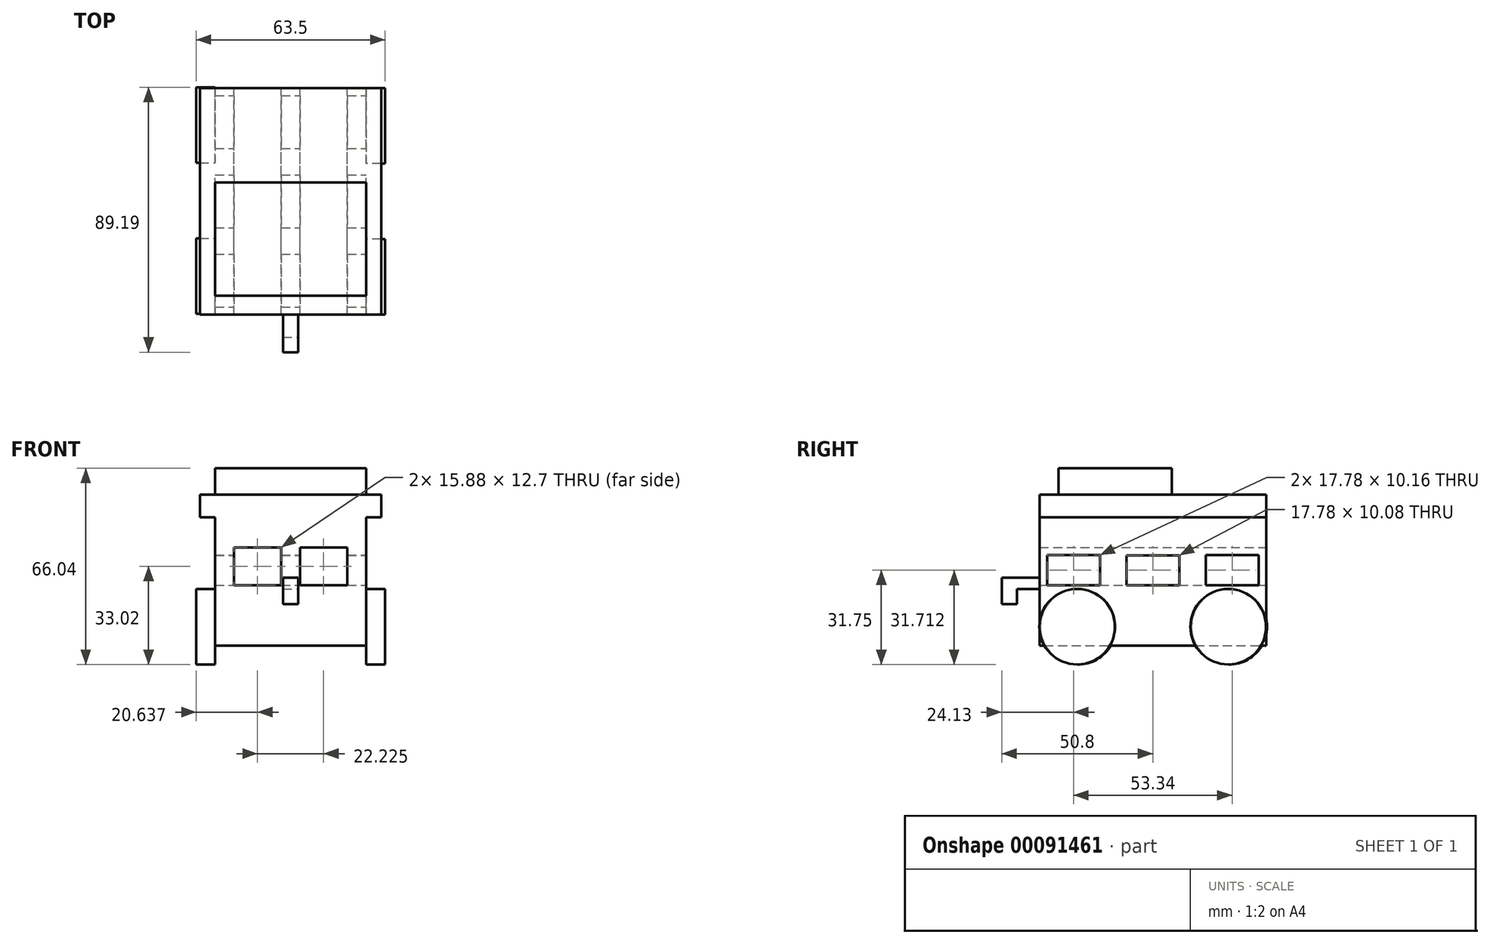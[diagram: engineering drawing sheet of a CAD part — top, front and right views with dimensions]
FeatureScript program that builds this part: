
annotation { "Feature Type Name" : "Feature", "Feature Type Description" : "" }
export const myFeature = defineFeature(function(context is Context, id is Id, definition is map)
    precondition{}
    {
        {
            var Q0;
            Q0=qCreatedBy(makeId("Front.planeOp"),FACE);
            var sketch = newSketch(context, id + "F0", { "sketchPlane" : qUnion([Q0])});
            skLineSegment(sketch, "E0", {"start": v(0, 50.8) * mm, "end": v(55.88, 50.8) * mm});
            skLineSegment(sketch, "E1", {"start": v(55.88, 50.8) * mm, "end": v(55.88, 43.18) * mm});
            skLineSegment(sketch, "E2", {"start": v(55.88, 43.18) * mm, "end": v(50.8, 43.18) * mm});
            skLineSegment(sketch, "E3", {"start": v(50.8, 43.18) * mm, "end": v(50.8, 0) * mm});
            skLineSegment(sketch, "E4", {"start": v(50.8, 0) * mm, "end": v(0, 0) * mm});
            skLineSegment(sketch, "E5", {"start": v(0, 0) * mm, "end": v(0, 43.18) * mm});
            skLineSegment(sketch, "E6", {"start": v(0, 43.18) * mm, "end": v(-5.08, 43.18) * mm});
            skLineSegment(sketch, "E7", {"start": v(-5.08, 43.18) * mm, "end": v(-5.08, 50.8) * mm});
            skLineSegment(sketch, "E8", {"start": v(-5.08, 50.8) * mm, "end": v(0, 50.8) * mm});
            skSolve(sketch);
        }
        {
            var Q0;
            Q0=makeQuery(id+"F0.imprint","IMPRINT",FACE,{"disambiguationData":[TD([[makeQuery(id+"F0.imprint","IMPRINT",EDGE,{"derivedFrom":sQuery(id+"F0.wireOp",EDGE,"E0")}),-1.0]])]});
            extrude(context, id + "F1", {"entities" : qUnion([Q0]), "depth" : 76.2 * mm});
        }
        {
            var Q0;
            Q0=makeQuery(id+"F1.opExtrude","SWEPT_FACE",FACE,{"disambiguationData":[OSD([sQuery(id+"F0.wireOp",EDGE,"E3")])]});
            var sketch = newSketch(context, id + "F2", { "sketchPlane" : qUnion([Q0])});
            skLineSegment(sketch, "E9.bottom", {"start": v(-73.66, 30.48) * mm, "end": v(-55.88, 30.48) * mm});
            skLineSegment(sketch, "E9.top", {"start": v(-73.66, 20.32) * mm, "end": v(-55.88, 20.32) * mm});
            skLineSegment(sketch, "E9.left", {"start": v(-73.66, 30.48) * mm, "end": v(-73.66, 20.32) * mm});
            skLineSegment(sketch, "E9.right", {"start": v(-55.88, 30.48) * mm, "end": v(-55.88, 20.32) * mm});
            skLineSegment(sketch, "E10.bottom", {"start": v(-46.99, 30.4) * mm, "end": v(-29.2, 30.4) * mm});
            skLineSegment(sketch, "E10.top", {"start": v(-46.99, 20.32) * mm, "end": v(-29.2, 20.32) * mm});
            skLineSegment(sketch, "E10.left", {"start": v(-46.99, 30.4) * mm, "end": v(-46.99, 20.32) * mm});
            skLineSegment(sketch, "E10.right", {"start": v(-29.21, 30.4) * mm, "end": v(-29.21, 20.32) * mm});
            skLineSegment(sketch, "E11.bottom", {"start": v(-20.32, 30.48) * mm, "end": v(-2.54, 30.48) * mm});
            skLineSegment(sketch, "E11.top", {"start": v(-20.32, 20.32) * mm, "end": v(-2.54, 20.32) * mm});
            skLineSegment(sketch, "E11.left", {"start": v(-20.32, 30.48) * mm, "end": v(-20.32, 20.32) * mm});
            skLineSegment(sketch, "E11.right", {"start": v(-2.54, 30.48) * mm, "end": v(-2.54, 20.32) * mm});
            skSolve(sketch);
        }
        {
            var Q0;
            Q0=makeQuery(id+"F2.imprint","IMPRINT",FACE,{"disambiguationData":[TD([[makeQuery(id+"F2.imprint","IMPRINT",EDGE,{"derivedFrom":sQuery(id+"F2.wireOp",EDGE,"E9.bottom")}),-1.0]])]});
            var Q1;
            Q1=makeQuery(id+"F2.imprint","IMPRINT",FACE,{"disambiguationData":[TD([[makeQuery(id+"F2.imprint","IMPRINT",EDGE,{"derivedFrom":sQuery(id+"F2.wireOp",EDGE,"E10.bottom")}),-1.0]])]});
            var Q2;
            Q2=makeQuery(id+"F2.imprint","IMPRINT",FACE,{"disambiguationData":[TD([[makeQuery(id+"F2.imprint","IMPRINT",EDGE,{"derivedFrom":sQuery(id+"F2.wireOp",EDGE,"E11.bottom")}),-1.0]])]});
            extrude(context, id + "F3", {"entities" : qUnion([Q0, Q1, Q2]), "operationType" : NewBodyOperationType.REMOVE, "oppositeDirection" : true, "depth" : 50.8 * mm});
        }
        {
            var Q0;
            Q0=makeQuery(id+"F1.opExtrude","SWEPT_FACE",FACE,{"disambiguationData":[OSD([sQuery(id+"F0.wireOp",EDGE,"E3")])]});
            var sketch = newSketch(context, id + "F4", { "sketchPlane" : qUnion([Q0])});
            skCircle(sketch, "E12", {"center": v(-63.53, 6.35) * mm, "radius": 12.7 * mm});
            skCircle(sketch, "E13", {"center": v(-12.73, 6.35) * mm, "radius": 12.7 * mm});
            skSolve(sketch);
        }
        {
            var Q0;
            Q0 = qSketchRegion(id + "F4", true);
            extrude(context, id + "F5", {"entities" : qUnion([Q0]), "depth" : 6.35 * mm});
        }
        {
            var Q0;
            Q0=makeQuery(id+"F1.opExtrude","SWEPT_FACE",FACE,{"disambiguationData":[OSD([sQuery(id+"F0.wireOp",EDGE,"E5")])]});
            var sketch = newSketch(context, id + "F6", { "sketchPlane" : qUnion([Q0])});
            skCircle(sketch, "E14", {"center": v(63.21, 6.35) * mm, "radius": 12.7 * mm});
            skCircle(sketch, "E15", {"center": v(12.41, 6.35) * mm, "radius": 12.7 * mm});
            skSolve(sketch);
        }
        {
            var Q0;
            Q0=makeQuery(id+"F1.opExtrude","CAP_FACE",FACE,{"disambiguationData":[OSD([sQuery(id+"F0.wireOp",EDGE,"E0"),sQuery(id+"F0.wireOp",EDGE,"E1"),sQuery(id+"F0.wireOp",EDGE,"E2"),sQuery(id+"F0.wireOp",EDGE,"E3"),sQuery(id+"F0.wireOp",EDGE,"E4"),sQuery(id+"F0.wireOp",EDGE,"E5"),sQuery(id+"F0.wireOp",EDGE,"E6"),sQuery(id+"F0.wireOp",EDGE,"E7"),sQuery(id+"F0.wireOp",EDGE,"E8")])],"isStart":true});
            var sketch = newSketch(context, id + "F7", { "sketchPlane" : qUnion([Q0])});
            skLineSegment(sketch, "E16.bottom", {"start": v(-44.45, 33.02) * mm, "end": v(-28.57, 33.02) * mm});
            skLineSegment(sketch, "E16.top", {"start": v(-44.45, 20.32) * mm, "end": v(-28.57, 20.32) * mm});
            skLineSegment(sketch, "E16.left", {"start": v(-44.45, 33.02) * mm, "end": v(-44.45, 20.32) * mm});
            skLineSegment(sketch, "E16.right", {"start": v(-28.57, 33.02) * mm, "end": v(-28.57, 20.32) * mm});
            skLineSegment(sketch, "E17.bottom", {"start": v(-22.22, 33.02) * mm, "end": v(-6.35, 33.02) * mm});
            skLineSegment(sketch, "E17.top", {"start": v(-22.22, 20.32) * mm, "end": v(-6.35, 20.32) * mm});
            skLineSegment(sketch, "E17.left", {"start": v(-22.22, 33.02) * mm, "end": v(-22.22, 20.32) * mm});
            skLineSegment(sketch, "E17.right", {"start": v(-6.35, 33.02) * mm, "end": v(-6.35, 20.32) * mm});
            skSolve(sketch);
        }
        {
            var Q0;
            Q0=makeQuery(id+"F7.imprint","IMPRINT",FACE,{"disambiguationData":[TD([[makeQuery(id+"F7.imprint","IMPRINT",EDGE,{"derivedFrom":sQuery(id+"F7.wireOp",EDGE,"E16.bottom")}),-1.0]])]});
            var Q1;
            Q1=makeQuery(id+"F7.imprint","IMPRINT",FACE,{"disambiguationData":[TD([[makeQuery(id+"F7.imprint","IMPRINT",EDGE,{"derivedFrom":sQuery(id+"F7.wireOp",EDGE,"E17.bottom")}),-1.0]])]});
            extrude(context, id + "F8", {"entities" : qUnion([Q0, Q1]), "operationType" : NewBodyOperationType.REMOVE, "oppositeDirection" : true, "depth" : 76.2 * mm});
        }
        {
            var Q0;
            Q0=makeQuery(id+"F1.opExtrude","SWEPT_FACE",FACE,{"disambiguationData":[OSD([sQuery(id+"F0.wireOp",EDGE,"E0"),sQuery(id+"F0.wireOp",EDGE,"E8")])]});
            var sketch = newSketch(context, id + "F9", { "sketchPlane" : qUnion([Q0])});
            skPoint(sketch, "E18.end.orphan", {"position": v(55.88, -38.1) * mm});
            skPoint(sketch, "E19.start.orphan", {"position": v(-5.08, -38.1) * mm});
            skLineSegment(sketch, "E20.bottom", {"start": v(0, -31.75) * mm, "end": v(50.8, -31.75) * mm});
            skLineSegment(sketch, "E20.top", {"start": v(0, -69.85) * mm, "end": v(50.8, -69.85) * mm});
            skLineSegment(sketch, "E20.left", {"start": v(0, -31.75) * mm, "end": v(0, -69.85) * mm});
            skLineSegment(sketch, "E20.right", {"start": v(50.8, -31.75) * mm, "end": v(50.8, -69.85) * mm});
            skSolve(sketch);
        }
        {
            var Q0;
            Q0=makeQuery(id+"F9.imprint","IMPRINT",FACE,{"disambiguationData":[TD([[makeQuery(id+"F9.imprint","IMPRINT",EDGE,{"derivedFrom":sQuery(id+"F9.wireOp",EDGE,"E20.bottom")}),-1.0]])]});
            extrude(context, id + "F10", {"entities" : qUnion([Q0]), "depth" : 8.9 * mm});
        }
        {
            var Q0;
            Q0=makeQuery(id+"F1.opExtrude","SWEPT_FACE",FACE,{"disambiguationData":[OSD([sQuery(id+"F0.wireOp",EDGE,"E3")])]});
            var sketch = newSketch(context, id + "F11", { "sketchPlane" : qUnion([Q0])});
            skLineSegment(sketch, "E21", {"start": v(-76.2, 22.86) * mm, "end": v(-88.9, 22.86) * mm});
            skLineSegment(sketch, "E22", {"start": v(-88.9, 22.86) * mm, "end": v(-88.9, 13.97) * mm});
            skLineSegment(sketch, "E23", {"start": v(-88.9, 13.97) * mm, "end": v(-83.82, 13.97) * mm});
            skLineSegment(sketch, "E24", {"start": v(-83.82, 13.97) * mm, "end": v(-83.82, 19.05) * mm});
            skLineSegment(sketch, "E25", {"start": v(-83.82, 19.05) * mm, "end": v(-76.2, 19.05) * mm});
            skLineSegment(sketch, "E26", {"start": v(-76.2, 19.05) * mm, "end": v(-76.2, 22.86) * mm});
            skSolve(sketch);
        }
        {
            var Q0;
            Q0=makeQuery(id+"F11.imprint","IMPRINT",FACE,{"disambiguationData":[TD([[makeQuery(id+"F11.imprint","IMPRINT",EDGE,{"derivedFrom":sQuery(id+"F11.wireOp",EDGE,"E21")}),1.0]])]});
            extrude(context, id + "F12", {"entities" : qUnion([Q0]), "operationType" : NewBodyOperationType.ADD, "oppositeDirection" : true, "depth" : 27.94 * mm});
        }
        {
            var Q0;
            Q0 = qSketchRegion(id + "F11", true);
            extrude(context, id + "F13", {"entities" : qUnion([Q0]), "operationType" : NewBodyOperationType.REMOVE, "oppositeDirection" : true, "depth" : 22.86 * mm});
        }
        {
            var Q0;
            Q0 = qSketchRegion(id + "F6", true);
            extrude(context, id + "F14", {"entities" : qUnion([Q0]), "depth" : 6.35 * mm});
        }
    });
